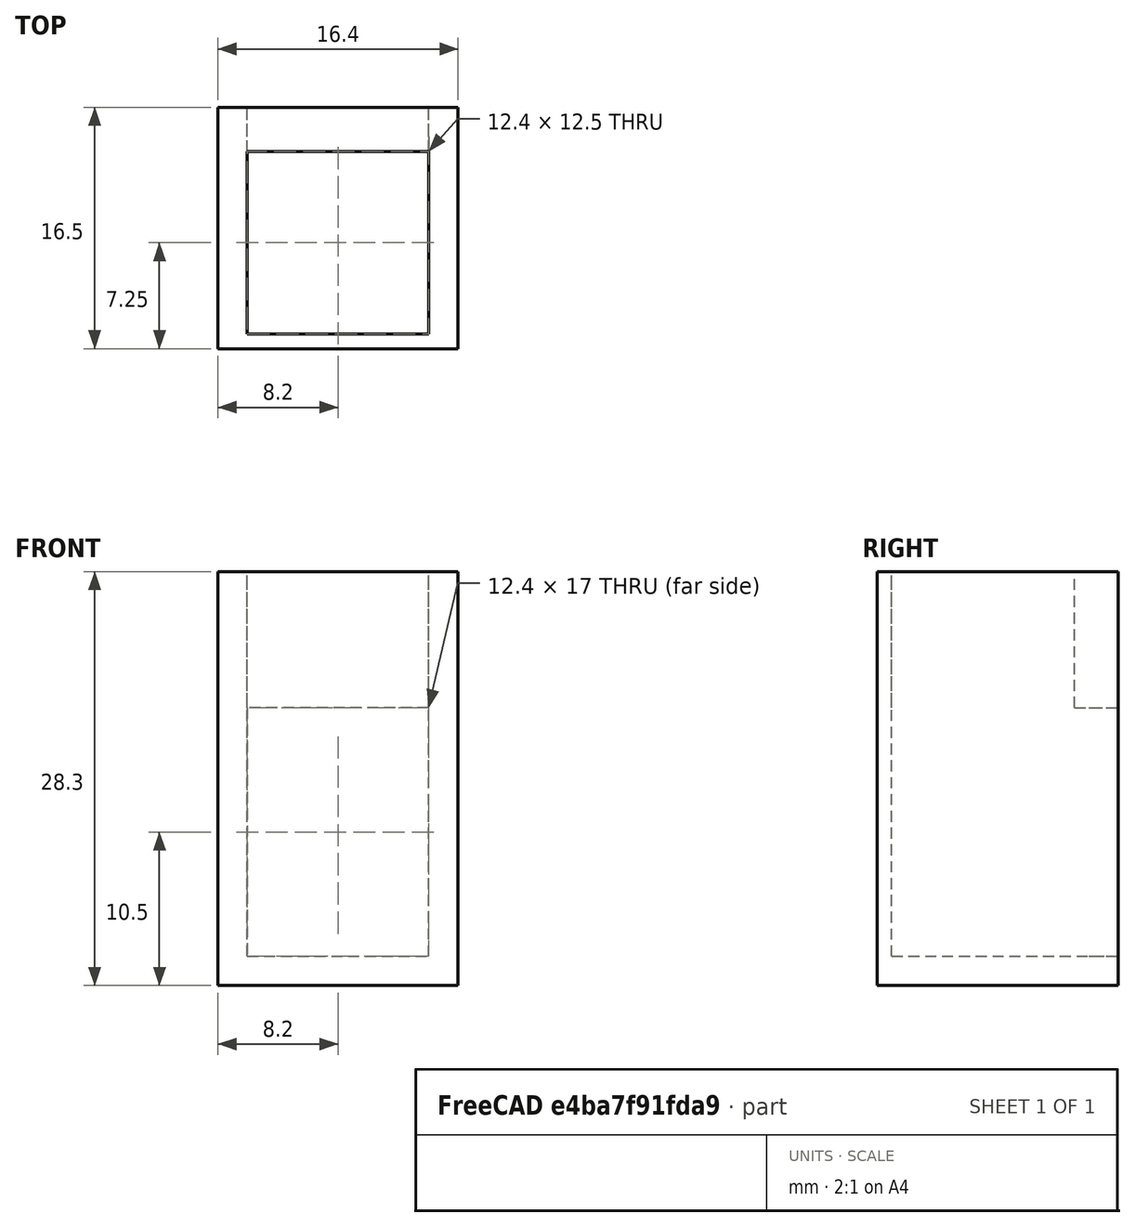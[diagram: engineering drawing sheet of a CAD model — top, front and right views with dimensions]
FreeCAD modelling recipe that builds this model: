
FCSTD DOCUMENT  (FreeCAD 0.20R28671 (Git))
Label: carcasa pot linear
License: All rights reserved
LicenseURL: http://en.wikipedia.org/wiki/All_rights_reserved
objects: TechDraw::DrawViewDimension×9, Sketcher::SketchObject×4, PartDesign::Pad×4, TechDraw::DrawProjGroupItem×2, PartDesign::Body×1, TechDraw::DrawSVGTemplate×1, Part::Refine×1, TechDraw::DrawProjGroup×1, TechDraw::DrawPage×1
note: 14 computed .brp shape members not serialized (recipe doc carries the construction recipe); baked Part::Feature solids carry a one-line shape summary decoded from their .brp

FEATURE [Sketcher::SketchObject] Sketch
  FullyConstrained = true
  MapMode = 5
  Support = -> [XY_Plane]
  sketch-geometry (11):
    g0: LineSegment StartX=0 StartY=0 StartZ=0 EndX=0 EndY=-14.5 EndZ=0
    g1: LineSegment StartX=0 StartY=-14.5 StartZ=0 EndX=16.4 EndY=-14.5 EndZ=0
    g2: LineSegment StartX=16.4 StartY=-14.5 StartZ=0 EndX=16.4 EndY=0 EndZ=0
    g3: LineSegment StartX=16.4 StartY=0 StartZ=0 EndX=14.4 EndY=0 EndZ=0
    g4: LineSegment StartX=14.4 StartY=0 StartZ=0 EndX=14.4 EndY=-13.5 EndZ=0
    g5: LineSegment StartX=14.4 StartY=-13.5 StartZ=0 EndX=2 EndY=-13.5 EndZ=0
    g6: LineSegment StartX=2 StartY=-13.5 StartZ=0 EndX=2 EndY=0 EndZ=0
    g7: LineSegment StartX=2 StartY=0 StartZ=0 EndX=0 EndY=0 EndZ=0
    g8: LineSegment StartX=14.4 StartY=-13.5 StartZ=0 EndX=14.4 EndY=-14.5 EndZ=0
    g9: LineSegment StartX=14.4 StartY=-13.5 StartZ=0 EndX=15.4 EndY=-13.5 EndZ=0
    g10: LineSegment StartX=15.4 StartY=-13.5 StartZ=0 EndX=16.4 EndY=-13.5 EndZ=0
  constraints (32):
    c: Coincident(g0,g-1)
    c: PointOnObject(g0,g-2)
    c: Coincident(g1,g0)
    c: Horizontal(g1)
    c: Coincident(g2,g1)
    c: PointOnObject(g2,g-1)
    c: Vertical(g2)
    c: Coincident(g3,g2)
    c: PointOnObject(g3,g-1)
    c: Coincident(g4,g3)
    c: Vertical(g4)
    c: Coincident(g5,g4)
    c: Horizontal(g5)
    c: Coincident(g6,g5)
    c: PointOnObject(g6,g-1)
    c: Vertical(g6)
    c: Coincident(g7,g6)
    c: Coincident(g7,g0)
    c: Equal(g3,g7)
    c: DistanceY(g6,g6) = 13.5
    c: DistanceX(g5,g5) = 12.4
    c: Coincident(g8,g4)
    c: PointOnObject(g8,g1)
    c: Vertical(g8)
    c: DistanceX(g3,g3) = 2
    c: Coincident(g9,g4)
    c: Horizontal(g9)
    c: Coincident(g10,g9)
    c: PointOnObject(g10,g2)
    c: Horizontal(g10)
    c: Equal(g9,g10)
    c: Equal(g8,g9)
FEATURE [PartDesign::Pad] Pad
  Direction = (0,0,1)
  Length = 17
  Length2 = 100
  Profile = -> Sketch
  Type = 0
FEATURE [Sketcher::SketchObject] Sketch001
  ExternalGeometry = -> [Pad]
  FullyConstrained = true
  MapMode = 5
  Placement = pos=(0,0,0) rot=(1,0,0;3.14159rad)
  Support = -> [Pad]
  sketch-geometry (4):
    g0: LineSegment StartX=0 StartY=14.5 StartZ=0 EndX=16.4 EndY=14.5 EndZ=0
    g1: LineSegment StartX=16.4 StartY=14.5 StartZ=0 EndX=16.4 EndY=0 EndZ=0
    g2: LineSegment StartX=16.4 StartY=0 StartZ=0 EndX=0 EndY=0 EndZ=0
    g3: LineSegment StartX=0 StartY=0 StartZ=0 EndX=0 EndY=14.5 EndZ=0
  constraints (10):
    c: Coincident(g0,g1)
    c: Coincident(g1,g2)
    c: Coincident(g2,g3)
    c: Coincident(g3,g0)
    c: Horizontal(g0)
    c: Horizontal(g2)
    c: Vertical(g1)
    c: Vertical(g3)
    c: Coincident(g0,g-3)
    c: Coincident(g1,g-4)
FEATURE [PartDesign::Pad] Pad001
  BaseFeature = -> Pad
  Direction = (0,0,-1)
  Length = 2
  Length2 = 100
  Profile = -> Sketch001
  Type = 0
FEATURE [Sketcher::SketchObject] Sketch002
  ExternalGeometry = -> [Pad001]
  FullyConstrained = true
  MapMode = 5
  Placement = pos=(0,0,17) rot=(0,0,1;0rad)
  Support = -> [Pad001]
  sketch-geometry (11):
    g0: LineSegment StartX=0 StartY=0 StartZ=0 EndX=16.4 EndY=0 EndZ=0
    g1: LineSegment StartX=16.4 StartY=0 StartZ=0 EndX=16.4 EndY=-14.5 EndZ=0
    g2: LineSegment StartX=16.4 StartY=-14.5 StartZ=0 EndX=0 EndY=-14.5 EndZ=0
    g3: LineSegment StartX=0 StartY=-14.5 StartZ=0 EndX=0 EndY=0 EndZ=0
    g4: LineSegment StartX=14.4 StartY=-13.5 StartZ=0 EndX=2 EndY=-13.5 EndZ=0
    g5: LineSegment StartX=2 StartY=-13.5 StartZ=0 EndX=2 EndY=-1 EndZ=0
    g6: LineSegment StartX=2 StartY=-1 StartZ=0 EndX=14.4 EndY=-1 EndZ=0
    g7: LineSegment StartX=14.4 StartY=-1 StartZ=0 EndX=14.4 EndY=-13.5 EndZ=0
    g8: LineSegment StartX=2 StartY=-1 StartZ=0 EndX=0 EndY=0 EndZ=0
    g9: LineSegment StartX=14.4 StartY=-13.5 StartZ=0 EndX=16.4 EndY=-14.5 EndZ=0
    g10: LineSegment StartX=14.4 StartY=-1 StartZ=0 EndX=16.4 EndY=0 EndZ=0
  constraints (27):
    c: Coincident(g0,g1)
    c: Coincident(g1,g2)
    c: Coincident(g2,g3)
    c: Coincident(g3,g0)
    c: Horizontal(g0)
    c: Horizontal(g2)
    c: Vertical(g1)
    c: Vertical(g3)
    c: Coincident(g0,g-1)
    c: Coincident(g1,g-3)
    c: Coincident(g4,g5)
    c: Coincident(g5,g6)
    c: Coincident(g6,g7)
    c: Coincident(g7,g4)
    c: Horizontal(g4)
    c: Horizontal(g6)
    c: Vertical(g5)
    c: Vertical(g7)
    c: Coincident(g4,g-4)
    c: Coincident(g8,g5)
    c: Coincident(g8,g0)
    c: Coincident(g9,g4)
    c: Coincident(g9,g1)
    c: Equal(g9,g8)
    c: Coincident(g10,g6)
    c: Coincident(g10,g0)
    c: Equal(g10,g8)
FEATURE [PartDesign::Pad] Pad002
  BaseFeature = -> Pad001
  Direction = (0,0,1)
  Length = 9.3
  Length2 = 100
  Profile = -> Sketch002
  Type = 0
FEATURE [Sketcher::SketchObject] Sketch003
  ExternalGeometry = -> [Pad002]
  FullyConstrained = true
  MapMode = 5
  Placement = pos=(0,0,0) rot=(0,0.707107,0.707107;3.14159rad)
  Support = -> [Pad002]
  sketch-geometry (8):
    g0: LineSegment StartX=-16.4 StartY=26.3 StartZ=0 EndX=0 EndY=26.3 EndZ=0
    g1: LineSegment StartX=0 StartY=26.3 StartZ=0 EndX=0 EndY=-2 EndZ=0
    g2: LineSegment StartX=0 StartY=-2 StartZ=0 EndX=-16.4 EndY=-2 EndZ=0
    g3: LineSegment StartX=-16.4 StartY=-2 StartZ=0 EndX=-16.4 EndY=26.3 EndZ=0
    g4: LineSegment StartX=-14.4 StartY=17 StartZ=0 EndX=-2 EndY=17 EndZ=0
    g5: LineSegment StartX=-2 StartY=17 StartZ=0 EndX=-2 EndY=0 EndZ=0
    g6: LineSegment StartX=-2 StartY=0 StartZ=0 EndX=-14.4 EndY=0 EndZ=0
    g7: LineSegment StartX=-14.4 StartY=0 StartZ=0 EndX=-14.4 EndY=17 EndZ=0
  constraints (20):
    c: Coincident(g0,g1)
    c: Coincident(g1,g2)
    c: Coincident(g2,g3)
    c: Coincident(g3,g0)
    c: Horizontal(g0)
    c: Horizontal(g2)
    c: Vertical(g1)
    c: Vertical(g3)
    c: Coincident(g0,g-3)
    c: Coincident(g1,g-4)
    c: Coincident(g4,g5)
    c: Coincident(g5,g6)
    c: Coincident(g6,g7)
    c: Coincident(g7,g4)
    c: Horizontal(g4)
    c: Horizontal(g6)
    c: Vertical(g5)
    c: Vertical(g7)
    c: Coincident(g4,g-5)
    c: Coincident(g5,g-6)
FEATURE [PartDesign::Pad] Pad003
  BaseFeature = -> Pad002
  Direction = (0,1,-2e-16)
  Length = 2
  Length2 = 100
  Profile = -> Sketch003
  ReferenceAxis = -> Sketch003 [N_Axis]
  Type = 0
FEATURE [PartDesign::Body] Body
  Group = -> [Sketch,Pad,Sketch001,Pad001,Sketch002,Pad002,Sketch003,Pad003]
  Origin = -> Origin
  Tip = -> Pad003
FEATURE [TechDraw::DrawSVGTemplate] Template
  EditableTexts = AUTHOR_NAME=Daniel García García; DATE=15-04-2022; DN=12; DOCUMENT_TYPE=Plano de Pieza; PN=17; REVISION=1; SCALE=2:1; SHEET=12/15; SIZE=A4; TITLELINE-1=Carcasa del potenciómetro lineal
  Height = 210
  Orientation = 1
  Width = 297
FEATURE [Part::Refine] Pad003001
  Source = -> Pad003
FEATURE [TechDraw::DrawProjGroupItem] ProjItem  label="Front"
  CoarseView = false
  Direction = (0,1,0)
  Focus = 100
  HardHidden = false
  IsoCount = 0
  IsoHidden = false
  IsoVisible = false
  LockPosition = true
  Perspective = false
  Rotation = 0
  RotationVector = (-1,0,0)
  Scale = 2
  ScaleType = 2
  SeamHidden = false
  SeamVisible = true
  SmoothHidden = false
  SmoothVisible = true
  Source = -> [Pad003001]
  Type = 0
  X = 0
  XDirection = (-1,0,0)
  Y = 0
FEATURE [TechDraw::DrawProjGroupItem] ProjItem001  label="Top"
  CoarseView = false
  Direction = (0,0,1)
  Focus = 100
  HardHidden = false
  IsoCount = 0
  IsoHidden = false
  IsoVisible = false
  LockPosition = true
  Perspective = false
  Rotation = 0
  RotationVector = (1,0,0)
  ScaleType = 2
  SeamHidden = false
  SeamVisible = true
  SmoothHidden = false
  SmoothVisible = true
  Source = -> [Pad003001]
  Type = 4
  X = 0
  XDirection = (-1,0,0)
  Y = -75.5429
FEATURE [TechDraw::DrawProjGroup] ProjGroup
  Anchor = -> ProjItem
  AutoDistribute = true
  LockPosition = true
  ProjectionType = 0
  Rotation = 0
  Scale = 2
  ScaleType = 2
  Source = -> [Pad003001]
  Views = -> [ProjItem,ProjItem001]
  X = 149.632
  Y = 146.343
  spacingX = 15
  spacingY = 15
FEATURE [TechDraw::DrawViewDimension] Dimension
  AngleOverride = false
  Arbitrary = false
  ArbitraryTolerances = false
  EqualTolerance = true
  ExtensionAngle = 0
  FormatSpec = %.2w
  FormatSpecOverTolerance = %+.2w
  FormatSpecUnderTolerance = %+.2w
  Inverted = false
  LineAngle = 0
  LockPosition = false
  MeasureType = 1
  OverTolerance = 0
  References2D = -> [ProjItem]
  Rotation = 0
  ScaleType = 0
  TheoreticalExact = false
  Type = 2
  UnderTolerance = 0
  X = -36.0974
  Y = 3.51883
FEATURE [TechDraw::DrawViewDimension] Dimension001
  AngleOverride = false
  Arbitrary = false
  ArbitraryTolerances = false
  EqualTolerance = true
  ExtensionAngle = 0
  FormatSpec = %.2w
  FormatSpecOverTolerance = %+.2w
  FormatSpecUnderTolerance = %+.2w
  Inverted = false
  LineAngle = 0
  LockPosition = false
  MeasureType = 1
  OverTolerance = 0
  References2D = -> [ProjItem]
  Rotation = 0
  ScaleType = 0
  TheoreticalExact = false
  Type = 2
  UnderTolerance = 0
  X = 28.7013
  Y = -4.8
FEATURE [TechDraw::DrawViewDimension] Dimension002
  AngleOverride = false
  Arbitrary = false
  ArbitraryTolerances = false
  EqualTolerance = true
  ExtensionAngle = 0
  FormatSpec = %.2w
  FormatSpecOverTolerance = %+.2w
  FormatSpecUnderTolerance = %+.2w
  Inverted = false
  LineAngle = 0
  LockPosition = false
  MeasureType = 1
  OverTolerance = 0
  References2D = -> [ProjItem]
  Rotation = 0
  ScaleType = 0
  TheoreticalExact = false
  Type = 1
  UnderTolerance = 0
  X = -0.679219
  Y = 39.9695
FEATURE [TechDraw::DrawViewDimension] Dimension003
  AngleOverride = false
  Arbitrary = false
  ArbitraryTolerances = false
  EqualTolerance = true
  ExtensionAngle = 0
  FormatSpec = %.2w
  FormatSpecOverTolerance = %+.2w
  FormatSpecUnderTolerance = %+.2w
  Inverted = false
  LineAngle = 0
  LockPosition = false
  MeasureType = 1
  OverTolerance = 0
  References2D = -> [ProjItem]
  Rotation = 0
  ScaleType = 0
  TheoreticalExact = false
  Type = 1
  UnderTolerance = 0
  X = 0
  Y = -37.7617
FEATURE [TechDraw::DrawViewDimension] Dimension004
  AngleOverride = false
  Arbitrary = false
  ArbitraryTolerances = false
  EqualTolerance = true
  ExtensionAngle = 0
  FormatSpec = %.2w
  FormatSpecOverTolerance = %+.2w
  FormatSpecUnderTolerance = %+.2w
  Inverted = false
  LineAngle = 0
  LockPosition = false
  MeasureType = 1
  OverTolerance = 0
  References2D = -> [ProjItem]
  Rotation = 0
  ScaleType = 0
  TheoreticalExact = false
  Type = 2
  UnderTolerance = 0
  X = 28.6636
  Y = -32.9695
FEATURE [TechDraw::DrawViewDimension] Dimension005
  AngleOverride = false
  Arbitrary = false
  ArbitraryTolerances = false
  EqualTolerance = true
  ExtensionAngle = 0
  FormatSpec = %.2w
  FormatSpecOverTolerance = %+.2w
  FormatSpecUnderTolerance = %+.2w
  Inverted = false
  LineAngle = 0
  LockPosition = false
  MeasureType = 1
  OverTolerance = 0
  References2D = -> [ProjItem001]
  Rotation = 0
  ScaleType = 0
  TheoreticalExact = false
  Type = 1
  UnderTolerance = 0
  X = 21.0964
  Y = -5.04762
FEATURE [TechDraw::DrawViewDimension] Dimension006
  AngleOverride = false
  Arbitrary = false
  ArbitraryTolerances = false
  EqualTolerance = true
  ExtensionAngle = 0
  FormatSpec = %.2w
  FormatSpecOverTolerance = %+.2w
  FormatSpecUnderTolerance = %+.2w
  Inverted = false
  LineAngle = 0
  LockPosition = false
  MeasureType = 1
  OverTolerance = 0
  References2D = -> [ProjItem001]
  Rotation = 0
  ScaleType = 0
  TheoreticalExact = false
  Type = 2
  UnderTolerance = 0
  X = -15.144
  Y = 28.7887
FEATURE [TechDraw::DrawViewDimension] Dimension007
  AngleOverride = false
  Arbitrary = false
  ArbitraryTolerances = false
  EqualTolerance = true
  ExtensionAngle = 0
  FormatSpec = %.2w
  FormatSpecOverTolerance = %+.2w
  FormatSpecUnderTolerance = %+.2w
  Inverted = false
  LineAngle = 0
  LockPosition = false
  MeasureType = 1
  OverTolerance = 0
  References2D = -> [ProjItem001]
  Rotation = 0
  ScaleType = 0
  TheoreticalExact = false
  Type = 2
  UnderTolerance = 0
  X = -15.5161
  Y = -18.8125
FEATURE [TechDraw::DrawViewDimension] Dimension008
  AngleOverride = false
  Arbitrary = false
  ArbitraryTolerances = false
  EqualTolerance = true
  ExtensionAngle = 0
  FormatSpec = %.2w
  FormatSpecOverTolerance = %+.2w
  FormatSpecUnderTolerance = %+.2w
  Inverted = false
  LineAngle = 0
  LockPosition = false
  MeasureType = 1
  OverTolerance = 0
  References2D = -> [ProjItem001]
  Rotation = 0
  ScaleType = 0
  TheoreticalExact = false
  Type = 2
  UnderTolerance = 0
  X = -26.8167
  Y = 2.87202
FEATURE [TechDraw::DrawPage] Page  label="Carcasa del potenciómetro"
  KeepUpdated = true
  NextBalloonIndex = 1
  ProjectionType = 0
  Template = -> Template
  Views = -> [ProjGroup,Dimension,Dimension001,Dimension002,Dimension003,Dimension004,Dimension005,Dimension006,Dimension007,Dimension008]
